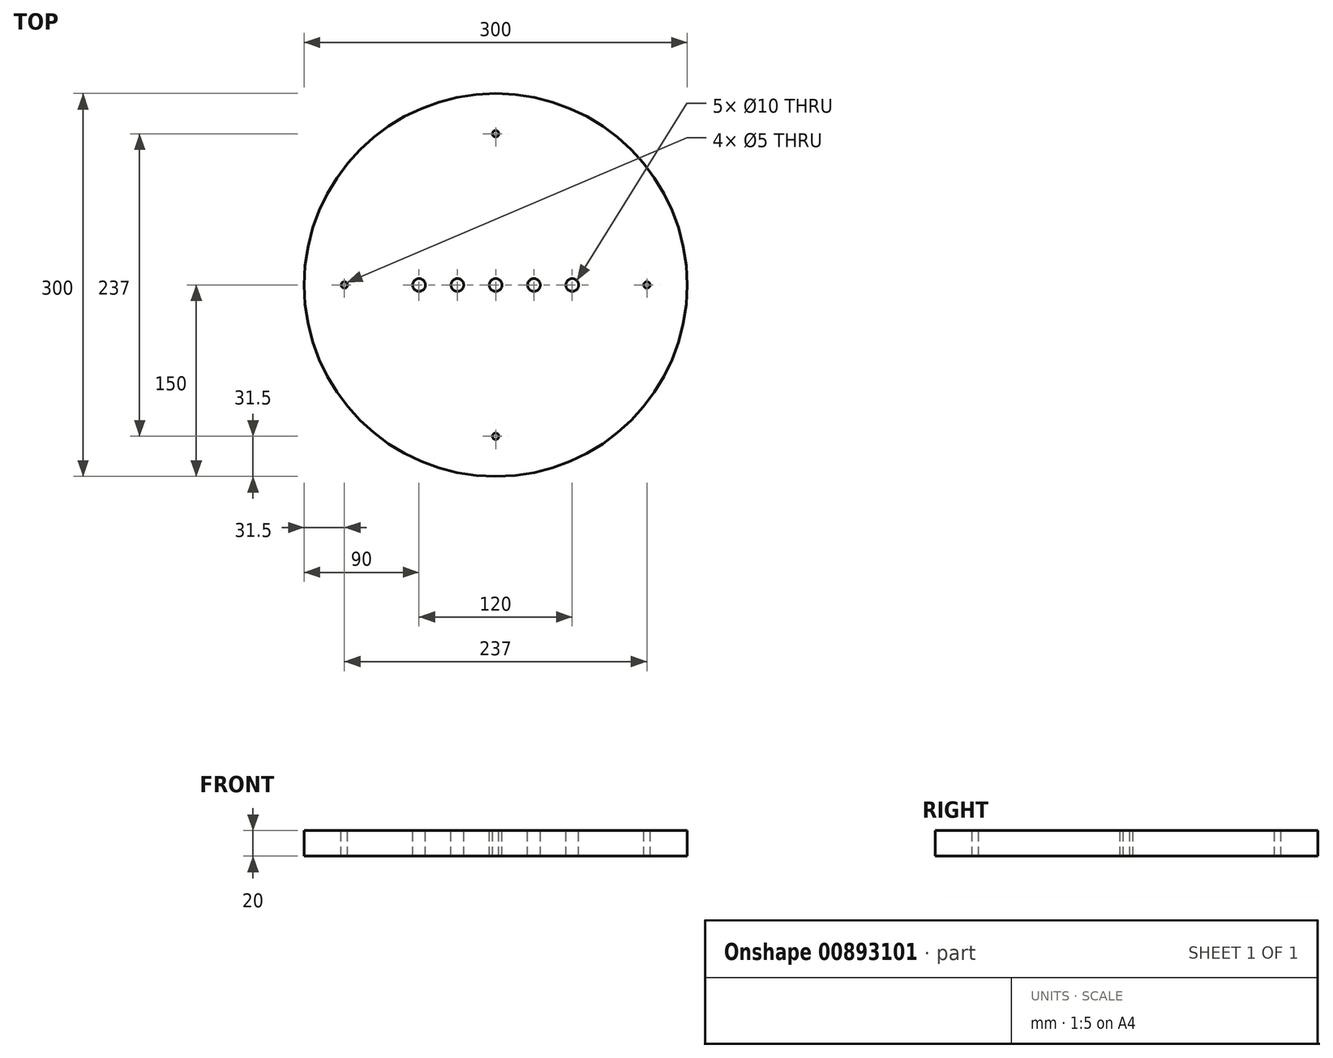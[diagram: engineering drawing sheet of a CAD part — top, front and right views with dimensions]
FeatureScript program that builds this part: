
annotation { "Feature Type Name" : "Feature", "Feature Type Description" : "" }
export const myFeature = defineFeature(function(context is Context, id is Id, definition is map)
    precondition{}
    {
        {
            var Q0;
            Q0=qCreatedBy(makeId("Top.planeOp"),FACE);
            var sketch = newSketch(context, id + "F0", { "sketchPlane" : qUnion([Q0])});
            skCircle(sketch, "E0", {"center": v(0, 0) * mm, "radius": 150 * mm});
            skSolve(sketch);
        }
        {
            var Q0;
            Q0=makeQuery(id+"F0.imprint","IMPRINT",FACE,{"disambiguationData":[TD([[makeQuery(id+"F0.imprint","IMPRINT",EDGE,{"derivedFrom":sQuery(id+"F0.wireOp",EDGE,"E0")}),1.0]])]});
            extrude(context, id + "F1", {"entities" : qUnion([Q0]), "depth" : 20 * mm, "offsetDistance" : 25 * mm});
        }
        {
            var Q0;
            Q0=makeQuery(id+"F1.opExtrude","CAP_FACE",FACE,{"disambiguationData":[OSD([sQuery(id+"F0.wireOp",EDGE,"E0")])],"isStart":false});
            var sketch = newSketch(context, id + "F2", { "sketchPlane" : qUnion([Q0])});
            skCircle(sketch, "E1", {"center": v(0, 0) * mm, "radius": 118.5 * mm});
            skCircle(sketch, "E2", {"center": v(0, 118.5) * mm, "radius": 2.5 * mm});
            skCircle(sketch, "E3", {"center": v(118.5, 0) * mm, "radius": 2.5 * mm});
            skCircle(sketch, "E4", {"center": v(0, -118.5) * mm, "radius": 2.5 * mm});
            skCircle(sketch, "E5", {"center": v(-118.5, 0) * mm, "radius": 2.5 * mm});
            skSolve(sketch);
        }
        {
            var Q0;
            {var subQ0=sQuery(id+"F2.wireOp",EDGE,"E2");var subQ1=sQuery(id+"F2.wireOp",EDGE,"E1");var subQ2=makeQuery(id+"F2.imprint","INTERSECT",VERTEX,{"disambiguationData":[OD(0.0)],"derivedFrom":[subQ1,subQ0]});Q0=makeQuery(id+"F2.imprint","IMPRINT",FACE,{"disambiguationData":[TD([[makeQuery(id+"F2.imprint","IMPRINT",EDGE,{"disambiguationData":[TD([[subQ2,-1.0]])],"derivedFrom":subQ1}),-1.0]])]});}
            var Q1;
            {var subQ0=sQuery(id+"F2.wireOp",EDGE,"E2");var subQ1=sQuery(id+"F2.wireOp",EDGE,"E1");var subQ2=makeQuery(id+"F2.imprint","INTERSECT",VERTEX,{"disambiguationData":[OD(0.0)],"derivedFrom":[subQ1,subQ0]});Q1=makeQuery(id+"F2.imprint","IMPRINT",FACE,{"disambiguationData":[TD([[makeQuery(id+"F2.imprint","IMPRINT",EDGE,{"disambiguationData":[TD([[subQ2,-1.0]])],"derivedFrom":subQ1}),1.0]])]});}
            var Q2;
            {var subQ0=sQuery(id+"F2.wireOp",EDGE,"E5");var subQ1=sQuery(id+"F2.wireOp",EDGE,"E1");var subQ2=makeQuery(id+"F2.imprint","INTERSECT",VERTEX,{"disambiguationData":[OD(0.0)],"derivedFrom":[subQ1,subQ0]});Q2=makeQuery(id+"F2.imprint","IMPRINT",FACE,{"disambiguationData":[TD([[makeQuery(id+"F2.imprint","IMPRINT",EDGE,{"disambiguationData":[TD([[subQ2,-1.0]])],"derivedFrom":subQ1}),-1.0]])]});}
            var Q3;
            {var subQ0=sQuery(id+"F2.wireOp",EDGE,"E5");var subQ1=sQuery(id+"F2.wireOp",EDGE,"E1");var subQ2=makeQuery(id+"F2.imprint","INTERSECT",VERTEX,{"disambiguationData":[OD(0.0)],"derivedFrom":[subQ1,subQ0]});Q3=makeQuery(id+"F2.imprint","IMPRINT",FACE,{"disambiguationData":[TD([[makeQuery(id+"F2.imprint","IMPRINT",EDGE,{"disambiguationData":[TD([[subQ2,-1.0]])],"derivedFrom":subQ1}),1.0]])]});}
            var Q4;
            {var subQ0=sQuery(id+"F2.wireOp",EDGE,"E3");var subQ1=sQuery(id+"F2.wireOp",EDGE,"E1");var subQ2=makeQuery(id+"F2.imprint","INTERSECT",VERTEX,{"disambiguationData":[OD(0.0)],"derivedFrom":[subQ1,subQ0]});Q4=makeQuery(id+"F2.imprint","IMPRINT",FACE,{"disambiguationData":[TD([[makeQuery(id+"F2.imprint","IMPRINT",EDGE,{"disambiguationData":[TD([[subQ2,1.0]])],"derivedFrom":subQ1}),1.0]])]});}
            var Q5;
            {var subQ0=sQuery(id+"F2.wireOp",EDGE,"E3");var subQ1=sQuery(id+"F2.wireOp",EDGE,"E1");var subQ2=makeQuery(id+"F2.imprint","INTERSECT",VERTEX,{"disambiguationData":[OD(0.0)],"derivedFrom":[subQ1,subQ0]});Q5=makeQuery(id+"F2.imprint","IMPRINT",FACE,{"disambiguationData":[TD([[makeQuery(id+"F2.imprint","IMPRINT",EDGE,{"disambiguationData":[TD([[subQ2,1.0]])],"derivedFrom":subQ1}),-1.0]])]});}
            var Q6;
            {var subQ0=sQuery(id+"F2.wireOp",EDGE,"E4");var subQ1=sQuery(id+"F2.wireOp",EDGE,"E1");var subQ2=makeQuery(id+"F2.imprint","INTERSECT",VERTEX,{"disambiguationData":[OD(0.0)],"derivedFrom":[subQ1,subQ0]});Q6=makeQuery(id+"F2.imprint","IMPRINT",FACE,{"disambiguationData":[TD([[makeQuery(id+"F2.imprint","IMPRINT",EDGE,{"disambiguationData":[TD([[subQ2,-1.0]])],"derivedFrom":subQ1}),1.0]])]});}
            var Q7;
            {var subQ0=sQuery(id+"F2.wireOp",EDGE,"E4");var subQ1=sQuery(id+"F2.wireOp",EDGE,"E1");var subQ2=makeQuery(id+"F2.imprint","INTERSECT",VERTEX,{"disambiguationData":[OD(0.0)],"derivedFrom":[subQ1,subQ0]});Q7=makeQuery(id+"F2.imprint","IMPRINT",FACE,{"disambiguationData":[TD([[makeQuery(id+"F2.imprint","IMPRINT",EDGE,{"disambiguationData":[TD([[subQ2,-1.0]])],"derivedFrom":subQ1}),-1.0]])]});}
            extrude(context, id + "F3", {"entities" : qUnion([Q0, Q1, Q2, Q3, Q4, Q5, Q6, Q7]), "operationType" : NewBodyOperationType.REMOVE, "endBound" : BoundingType.THROUGH_ALL, "oppositeDirection" : true, "depth" : 25 * mm, "offsetDistance" : 25 * mm});
        }
        {
            var Q0;
            Q0=makeQuery(id+"F1.opExtrude","CAP_FACE",FACE,{"disambiguationData":[OSD([sQuery(id+"F0.wireOp",EDGE,"E0")])],"isStart":false});
            var sketch = newSketch(context, id + "F4", { "sketchPlane" : qUnion([Q0])});
            skCircle(sketch, "E6", {"center": v(0, 0) * mm, "radius": 5 * mm});
            skCircle(sketch, "E7", {"center": v(30, 0) * mm, "radius": 5 * mm});
            skCircle(sketch, "E8", {"center": v(60, 0) * mm, "radius": 5 * mm});
            skCircle(sketch, "E9", {"center": v(-30, 0) * mm, "radius": 5 * mm});
            skCircle(sketch, "E10", {"center": v(-60, 0) * mm, "radius": 5 * mm});
            skSolve(sketch);
        }
        {
            var Q0;
            Q0=makeQuery(id+"F4.imprint","IMPRINT",FACE,{"disambiguationData":[TD([[makeQuery(id+"F4.imprint","IMPRINT",EDGE,{"derivedFrom":sQuery(id+"F4.wireOp",EDGE,"E6")}),1.0]])]});
            var Q1;
            Q1=makeQuery(id+"F4.imprint","IMPRINT",FACE,{"disambiguationData":[TD([[makeQuery(id+"F4.imprint","IMPRINT",EDGE,{"derivedFrom":sQuery(id+"F4.wireOp",EDGE,"E7")}),1.0]])]});
            var Q2;
            Q2=makeQuery(id+"F4.imprint","IMPRINT",FACE,{"disambiguationData":[TD([[makeQuery(id+"F4.imprint","IMPRINT",EDGE,{"derivedFrom":sQuery(id+"F4.wireOp",EDGE,"E8")}),1.0]])]});
            var Q3;
            Q3=makeQuery(id+"F4.imprint","IMPRINT",FACE,{"disambiguationData":[TD([[makeQuery(id+"F4.imprint","IMPRINT",EDGE,{"derivedFrom":sQuery(id+"F4.wireOp",EDGE,"E9")}),1.0]])]});
            var Q4;
            Q4=makeQuery(id+"F4.imprint","IMPRINT",FACE,{"disambiguationData":[TD([[makeQuery(id+"F4.imprint","IMPRINT",EDGE,{"derivedFrom":sQuery(id+"F4.wireOp",EDGE,"E10")}),1.0]])]});
            extrude(context, id + "F5", {"entities" : qUnion([Q0, Q1, Q2, Q3, Q4]), "operationType" : NewBodyOperationType.REMOVE, "endBound" : BoundingType.THROUGH_ALL, "oppositeDirection" : true, "depth" : 25 * mm, "offsetDistance" : 25 * mm});
        }
    });
